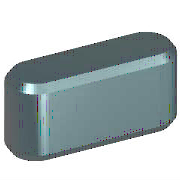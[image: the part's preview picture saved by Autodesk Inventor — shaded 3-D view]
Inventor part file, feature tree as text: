
AUTODESK INVENTOR PART (.ipt)
format: ipt  version: 2025 (Build 290162000, 162)  size: 136,192 bytes
history: native  units: mm (DEFAULTED — no unit token found)
features: plane x3, extrude x1
ambient origin geometry x8: Origin, YZ Plane, XZ Plane, XY Plane, X Axis, Y Axis, Z Axis, Center Point
bodies: Solid1 (feature_tree)
feature tree (4):
  plane  "Work Plane1"
  plane  "Work Plane2"
  extrude  "轴承体1"  Depth=6.0mm
  plane  "Work Plane3"
